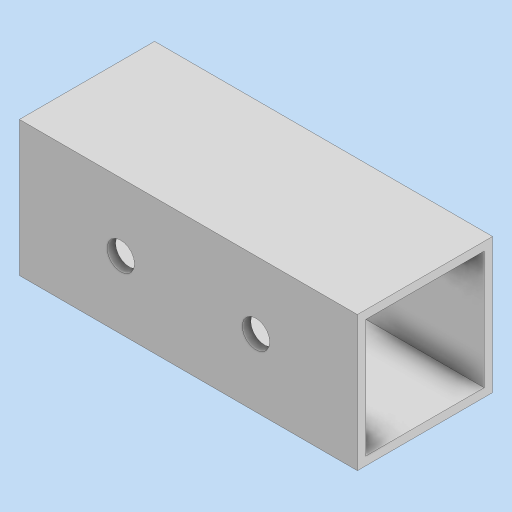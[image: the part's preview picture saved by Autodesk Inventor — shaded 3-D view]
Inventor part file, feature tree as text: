
AUTODESK INVENTOR PART (.ipt)
format: ipt  version: 2024 (Build 280153000, 153)  size: 120,320 bytes
history: native  units: in
note: dims shown in document units (in); Inventor stores cm internally (conversion verified against a paired STEP export)
features: extrude x2, sketch x2, projected_geometry x1
ambient origin geometry x8: Origin, YZ Plane, XZ Plane, XY Plane, X Axis, Y Axis, Z Axis, Center Point
bodies: Solid1 (feature_tree)
feature tree (5):
  extrude  "Extrusion1"  Depth=1.0in
  extrude  "Extrusion3"  Depth=2.5in TaperAngle=0.0deg
  sketch  "Sketch1"  dims[d0=1.0in d1=1.0in]
  sketch  "Sketch3"  dims[d2=0.0625in d3=2.5in d4=0.0in d14=0.203in d15=0.203in d16=0.5in d17=1.0in d18=1.0in d19=0.0in d20=0.5in]
  projected_geometry  "Projected Loop1"
